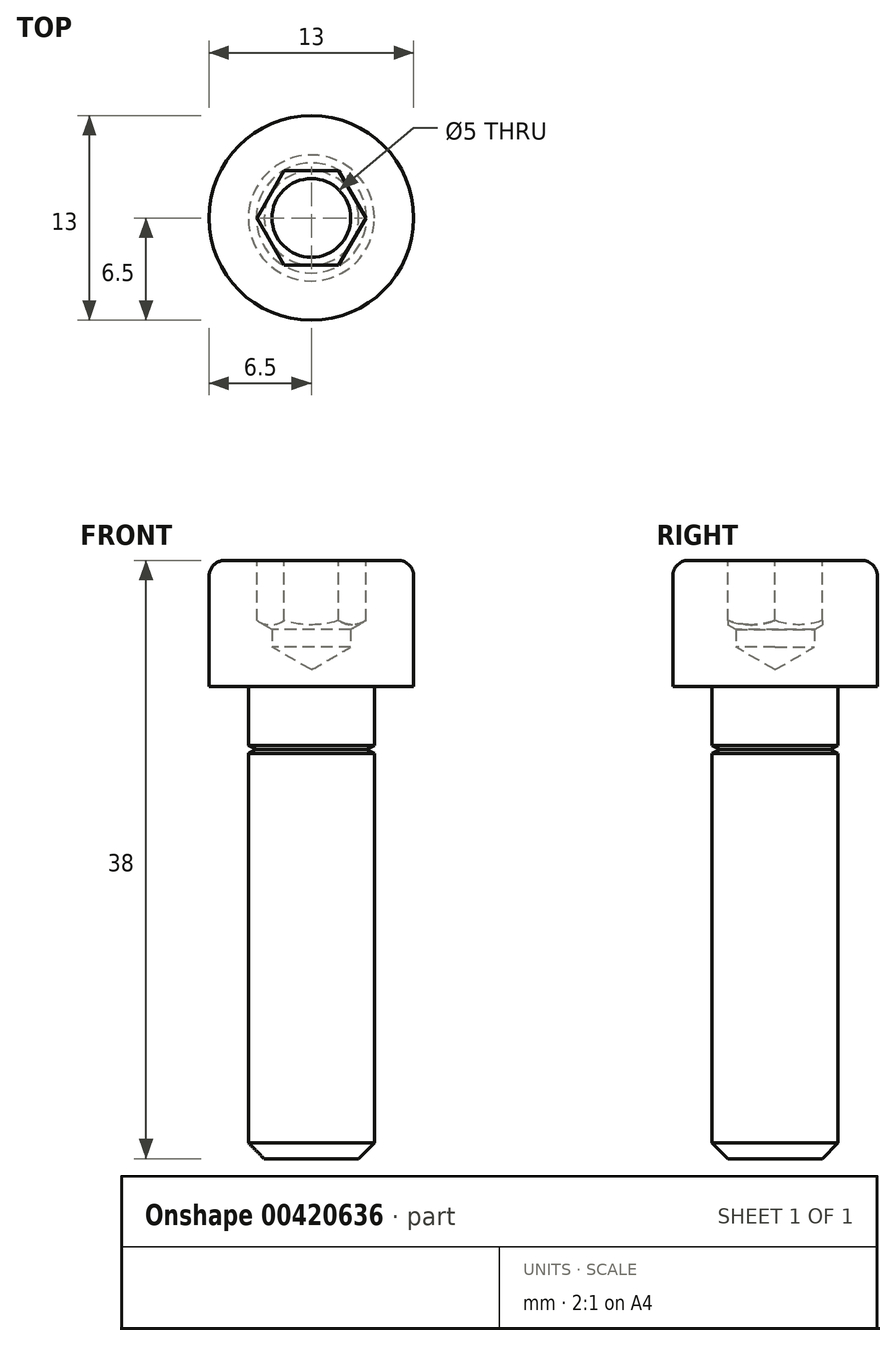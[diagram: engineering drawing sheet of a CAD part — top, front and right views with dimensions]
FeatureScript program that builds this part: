
annotation { "Feature Type Name" : "Feature", "Feature Type Description" : "" }
export const myFeature = defineFeature(function(context is Context, id is Id, definition is map)
    precondition{}
    {
        {
            var Q0;
            Q0=qCreatedBy(makeId("Front.planeOp"),FACE);
            var sketch = newSketch(context, id + "F0", { "sketchPlane" : qUnion([Q0])});
            skLineSegment(sketch, "E0", {"start": v(0, 0) * mm, "end": v(0, 36.66) * mm, "construction": true});
            skLineSegment(sketch, "E1", {"start": v(0, 0) * mm, "end": v(-4, 0) * mm});
            skLineSegment(sketch, "E2", {"start": v(-4, 0) * mm, "end": v(-4, 30) * mm, "construction": true});
            skLineSegment(sketch, "E3", {"start": v(-4, 30) * mm, "end": v(-6.5, 30) * mm});
            skLineSegment(sketch, "E4", {"start": v(-6.5, 30) * mm, "end": v(-6.5, 38) * mm});
            skLineSegment(sketch, "E5", {"start": v(-6.5, 38) * mm, "end": v(0, 38) * mm, "construction": true});
            skLineSegment(sketch, "E6", {"start": v(-2.5, 38) * mm, "end": v(-2.5, 32.5) * mm});
            skLineSegment(sketch, "E7", {"start": v(-2.5, 32.5) * mm, "end": v(0, 31.06) * mm});
            skLineSegment(sketch, "E8", {"start": v(0, 31.06) * mm, "end": v(0, 0) * mm});
            skLineSegment(sketch, "E9", {"start": v(-2.5, 38) * mm, "end": v(-6.5, 38) * mm});
            skLineSegment(sketch, "E10", {"start": v(-4, 26.25) * mm, "end": v(-3.5, 26) * mm});
            skLineSegment(sketch, "E11", {"start": v(-3.5, 26) * mm, "end": v(-4, 25.75) * mm});
            skLineSegment(sketch, "E12", {"start": v(-4, 25.75) * mm, "end": v(-4, 0) * mm});
            skLineSegment(sketch, "E13", {"start": v(-4, 26.25) * mm, "end": v(-4, 30) * mm});
            skSolve(sketch);
        }
        {
            var Q0;
            Q0=qSketchRegion(id+"F0",true);
            var Q1;
            Q1=sQuery(id+"F0.wireOp",EDGE,"E0");
            revolve(context, id + "F1", {"entities" : qUnion([Q0]), "axis" : qUnion([Q1]), "revolveType" : RevolveType.FULL});
        }
        {
            var Q0;
            Q0=makeQuery(id+"F1.opRevolve","SWEPT_EDGE",EDGE,{"disambiguationData":[OSD([sQuery(id+"F0.wireOp",EDGE,"E4"),sQuery(id+"F0.wireOp",EDGE,"E9")])]});
            fillet(context, id + "F2", {"entities" : qUnion([Q0]), "radius" : 1 * mm, "tangentPropagation" : true, "allowEdgeOverflow" : false});
        }
        {
            var Q0;
            Q0=makeQuery(id+"F1.opRevolve","SWEPT_EDGE",EDGE,{"disambiguationData":[OSD([sQuery(id+"F0.wireOp",EDGE,"E1"),sQuery(id+"F0.wireOp",EDGE,"E2")])]});
            chamfer(context, id + "F3", {"entities" : qUnion([Q0]), "width" : 1 * mm, "tangentPropagation" : true});
        }
        {
            var Q0;
            Q0=makeQuery(id+"F1.opRevolve","SWEPT_FACE",FACE,{"disambiguationData":[OSD([sQuery(id+"F0.wireOp",EDGE,"E9")])]});
            var sketch = newSketch(context, id + "F4", { "sketchPlane" : qUnion([Q0])});
            skCircle(sketch, "E14.cCircle", {"center": v(0, 0) * mm, "radius": 3 * mm, "construction": true});
            skLineSegment(sketch, "E14.0", {"start": v(1.73, -3) * mm, "end": v(-1.73, -3) * mm});
            skLineSegment(sketch, "E14.1", {"start": v(-1.73, -3) * mm, "end": v(-3.46, 0) * mm});
            skLineSegment(sketch, "E14.2", {"start": v(-3.46, 0) * mm, "end": v(-1.73, 3) * mm});
            skLineSegment(sketch, "E14.3", {"start": v(-1.73, 3) * mm, "end": v(1.73, 3) * mm});
            skLineSegment(sketch, "E14.4", {"start": v(1.73, 3) * mm, "end": v(3.46, 0) * mm});
            skLineSegment(sketch, "E14.5", {"start": v(3.46, 0) * mm, "end": v(1.73, -3) * mm});
            skPoint(sketch, "E14.0.midPoint", {"position": v(0, -3) * mm});
            skSolve(sketch);
        }
        {
            var Q0;
            Q0=qSketchRegion(id+"F4",true);
            extrude(context, id + "F5", {"entities" : qUnion([Q0]), "operationType" : NewBodyOperationType.REMOVE, "oppositeDirection" : true, "depth" : 2.88 * mm});
        }
        {
            var Q0;
            Q0=makeQuery(id+"F5.boolean.opBoolean","INTERSECT",EDGE,{"derivedFrom":[makeQuery(id+"F1.opRevolve","SWEPT_FACE",FACE,{"disambiguationData":[OSD([sQuery(id+"F0.wireOp",EDGE,"E6")])]}),makeQuery(id+"F5.opExtrude","CAP_FACE",FACE,{"disambiguationData":[OSD([sQuery(id+"F4.wireOp",EDGE,"E14.0"),sQuery(id+"F4.wireOp",EDGE,"E14.1"),sQuery(id+"F4.wireOp",EDGE,"E14.2"),sQuery(id+"F4.wireOp",EDGE,"E14.3"),sQuery(id+"F4.wireOp",EDGE,"E14.4"),sQuery(id+"F4.wireOp",EDGE,"E14.5")])],"isStart":false})]});
            chamfer(context, id + "F6", {"entities" : qUnion([Q0]), "chamferType" : ChamferType.OFFSET_ANGLE, "width" : 1.5 * mm, "oppositeDirection" : false, "angle" : 60 * degree, "tangentPropagation" : true});
        }
    });
